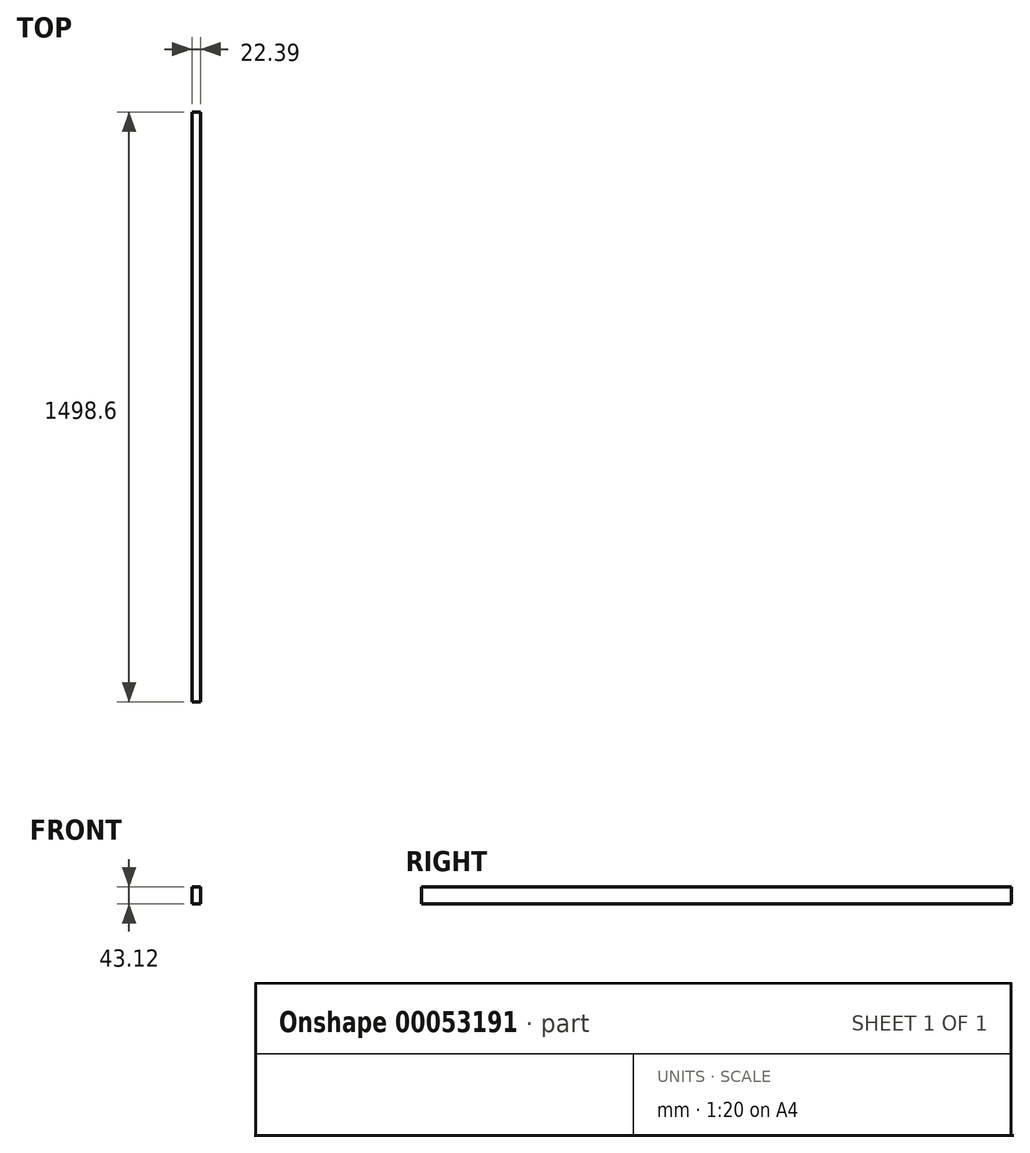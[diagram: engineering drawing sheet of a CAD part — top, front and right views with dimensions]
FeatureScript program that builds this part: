
annotation { "Feature Type Name" : "Feature", "Feature Type Description" : "" }
export const myFeature = defineFeature(function(context is Context, id is Id, definition is map)
    precondition{}
    {
        {
            var Q0;
            Q0=qCreatedBy(makeId("Front.planeOp"),FACE);
            var sketch = newSketch(context, id + "F0", { "sketchPlane" : qUnion([Q0])});
            skLineSegment(sketch, "E0.bottom", {"start": v(-119.3, 43.12) * mm, "end": v(-96.9, 43.12) * mm});
            skLineSegment(sketch, "E0.top", {"start": v(-119.3, 0) * mm, "end": v(-96.9, 0) * mm});
            skLineSegment(sketch, "E0.left", {"start": v(-119.3, 43.12) * mm, "end": v(-119.3, 0) * mm});
            skLineSegment(sketch, "E0.right", {"start": v(-96.9, 43.12) * mm, "end": v(-96.9, 0) * mm});
            skSolve(sketch);
        }
        {
            var Q0;
            Q0=makeQuery(id+"F0.imprint","IMPRINT",FACE,{"disambiguationData":[TD([[makeQuery(id+"F0.imprint","IMPRINT",EDGE,{"derivedFrom":sQuery(id+"F0.wireOp",EDGE,"E0.bottom")}),-1.0]])]});
            extrude(context, id + "F1", {"entities" : qUnion([Q0]), "oppositeDirection" : true, "depth" : 1498.6 * mm});
        }
    });
